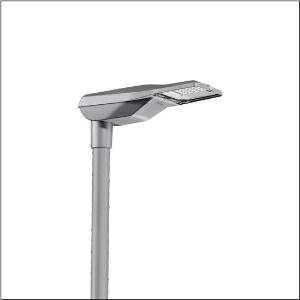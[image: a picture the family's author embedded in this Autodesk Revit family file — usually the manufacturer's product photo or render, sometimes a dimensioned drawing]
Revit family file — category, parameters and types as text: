
# Revit family: streetlight_sl_21_iq_micro___st1_0ab_5xe1m31d08cb_a4c0
name_source: partatom
category: Lighting Fixtures
units: mm (PartAtom-declared; Revit-internal decimal feet)

## family parameters
Cut with Voids When Loaded = No
Host = Face
Light Source = No
Part Type = Normal
Room Calculation Point = No
Round Connector Dimension = Use Diameter
Shared = No

## types (1)
- --- (1 x LED, 2520 lm, 19.4 W, 3000K)
    Apparent Load = 19 VA
    CIE Flux Codes = 38 73 97 100 100
    Color Rendering = 70
    Color Temperature = 3000K
    Default Elevation = 1800 mm
    Description = Streetlight SL 21 iQ micro, mast luminaire, primary light control with lens, of PMMA, primary optical cover: cover, of toughened safety glass, transparent, light distribution: ST1.0aB, light emission: direct distribution, primary light characteristic: asymmetric, installation type: post-top, side-entry, LED, High Power LED, rated luminous flux: 2.520lm, luminous efficacy: 130lm/W, light colour: 730, colour temperature: 3000K, control gear: iQ-Comfort, control: Auto-Match, Temp-Guard, Lumen-Switch, Night-Set, Smart-Wire, Light-Fading, Desk-Remote (wireless, voltage-free reading and setting of iQ features in the workshop via application-optimized NFC function/RFID function), optimised constant luminous flux control (CLO 2.0), pre-setting: linear dimming characteristic, mains connection: 220..240V, AC, 50/60Hz, start of lifetime: 19W, end of service life: 20W, reduction: 10W, luminaire housing, of diecast aluminium, powder-coated, Siteco® metallic grey (DB 702S), corrosivity category C5 high according to DIN EN ISO 12944, please order mast flange separately, inclination adjustable: 0°, 5°, 10°, 15°, sealing non-destructively replaceable, multi-level sealing system, length: 528mm, width: 235mm, height: 110mm, mast flange for spigot size: 42mm (side-entry): 5XC10008XM4, 60/48mm (side-entry/post-top): 5XC10108XM2, 76/60mm (side-entry/post-top): 5XC10108XM1, protection rating (complete): IP66, insulation class (complete): insulation class II (safety insulation), certification: CE, ENEC, ENEC+, VDE, impact resistance: IK10, permissible operating ambient temperature for outdoor applications: -40..+50°C, standard-compliant lighting for roads and squares, packaging unit: 1 piece

Light Distribution: ST1.0aB
    Height = 110 mm
    Lamp = 1 x LED
    Lamp Light Flux = 2520 lm
    Lamp Power = 19.4 W
    Lamp count = 1
    Length = 528 mm
    Luminous efficacy = 130 lm/W
    Manufacturer = Siteco
    ModVariant = No
    Model = 5XE1M31D08CB
    Number of Poles = 1
    OnlyDefault = Yes
    Power Factor = 1
    Product Name = Streetlight SL 21 iQ micro | ST1.0aB
    Product group = mast luminaire | pylon top
    ProductGroupID = 6100
    Protection Class = Protection class II
    Protection Degree = IP 66
    RLX_Detail_Level = 1
    RLX_Emergency_Light_Flux = 0 lm
    RLX_Emergency_Type = 0
    RLX_Emergency_Type_DB = No
    RlxData = <blob elided: 98281 chars, md5=05f6e42c>
    Socket = socket
    Standby Power = 0 W
    System Light Flux = 2520 lm
    System Power = 19 W
    Type Comments = factory setting: luminous flux: 100 % | dim-lin: 254 | 387 mA
    Type Image = l_1006881.jpg
    URL = http://relux.com
    VarID = @adj_141457
    Voltage = 0 V
    Weight = 0.00 kg
    Width = 235 mm

## geometry (parser evidence)
native form markers: Blend x4, Sweep x12
no freeform markers — native parametric forms only
